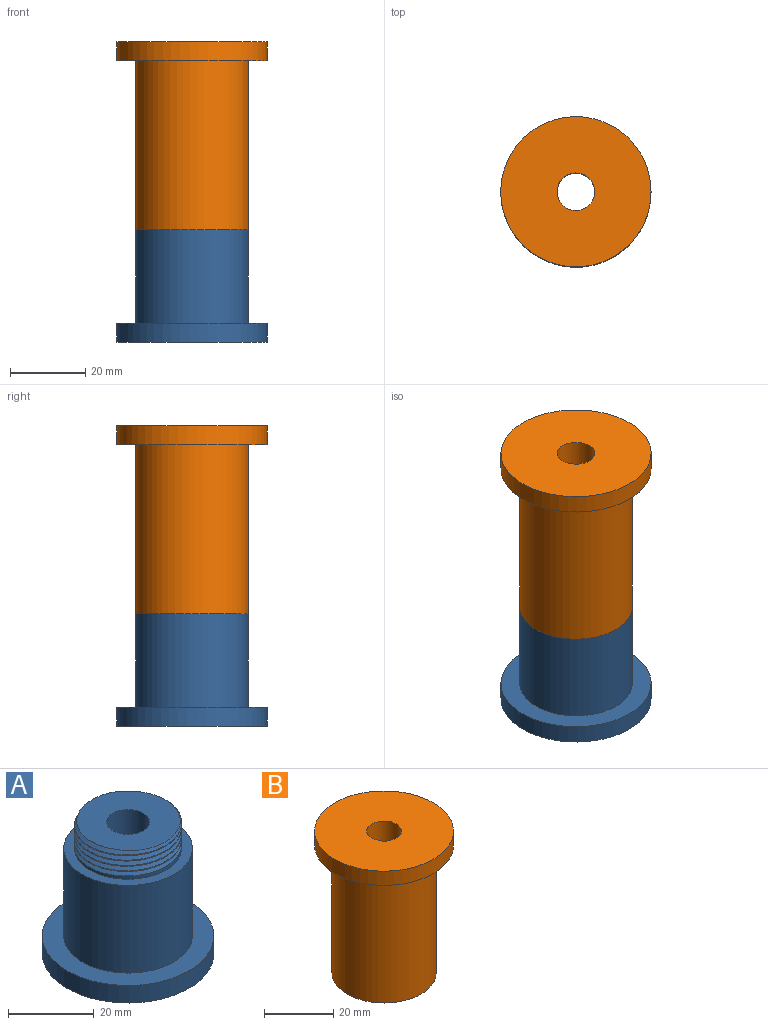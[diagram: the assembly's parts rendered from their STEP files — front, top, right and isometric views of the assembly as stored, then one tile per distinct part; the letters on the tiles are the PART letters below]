
ASSEMBLY  parts=2 mates=1
PART A: 11 faces, bbox 40.7x40.7x39 mm
  f0: cylinder r=12.5mm len=25mm, axis (0,0,-1), area 137.1mm2, adj f5,f7,f8,f9,f10
  f1: cylinder r=20mm len=40mm, axis (0,0,-1), area 628.3mm2, adj f2,f3
  f2: plane 40x40mm, normal (0,0,1), area 549.8mm2, adj f1,f6
  f3: plane 40x40mm, normal (0,0,-1), area 1178.1mm2, adj f1,f4
  f4: cylinder r=5mm len=37.5mm, axis (0,0,-1), area 1178.1mm2, adj f3,f5
  f5: plane 24.9x24.89mm, normal (0,0,1), area 378mm2, adj f0,f4,f9,f10
  f6: cylinder r=15mm len=30mm, axis (0,0,-1), area 2356.2mm2, adj f2,f7
  f7: plane 30x30mm, normal (0,0,1), area 216mm2, adj f0,f6
  f8: plane 1.25x1.08mm, normal (0,1,0), area 0.7mm2, adj f0,f9,f10
  f9: bspline ~28.87x25mm, area 451mm2, adj f0,f5,f8,f10
  f10: bspline ~28.87x25mm, area 410.9mm2, adj f0,f5,f8,f9
PART B: 11 faces, bbox 40.7x40.7x50.7 mm
  f0: cylinder r=15mm len=45mm, axis (0,0,1), area 4241.2mm2, adj f5,f7
  f1: cylinder r=5mm len=42.5mm, axis (0,0,1), area 1335.2mm2, adj f2,f3
  f2: plane 25.9x25.89mm, normal (0,0,-1), area 416.6mm2, adj f1,f4,f8,f9
  f3: plane 40x40mm, normal (0,0,1), area 1178.1mm2, adj f1,f6
  f4: cylinder r=13mm len=26mm, axis (0,0,1), area 144.8mm2, adj f2,f5,f8,f9,f10
  f5: plane 30x30mm, normal (0,0,-1), area 175.9mm2, adj f0,f4
  f6: cylinder r=20mm len=40mm, axis (0,0,1), area 628.3mm2, adj f3,f7
  f7: plane 40x40mm, normal (0,0,-1), area 549.8mm2, adj f0,f6
  f8: bspline ~30.02x26mm, area 469.7mm2, adj f2,f4,f9,f10
  f9: bspline ~30.02x26mm, area 428mm2, adj f2,f4,f8,f10
  f10: plane 1.25x1.08mm, normal (0,-1,0), area 0.7mm2, adj f4,f8,f9
PLACE A t=(-10.19,-19.83,-88.29)mm
PLACE B t=(-10.19,-19.83,-88.29)mm
MATE cylindrical B.f0 <-> A.f6  axis (0,0,1) through (-10.19,-19.83,-35.79)mm
